FCSTD DOCUMENT  (FreeCAD 1.0R39109 (Git))
Label: Vista frontal
License: All rights reserved
LicenseURL: https://en.wikipedia.org/wiki/All_rights_reserved
objects: TechDraw::DrawSVGTemplate×1, TechDraw::DrawPage×1, Sketcher::SketchObject×1
note: 2 computed .brp shape members not serialized (recipe doc carries the construction recipe); baked Part::Feature solids carry a one-line shape summary decoded from their .brp

FEATURE [TechDraw::DrawSVGTemplate] Template  label="Plantilla"
  EditableTexts = approval_person=N/A; creator=Carlos E.; date_of_issue=11/3/25; document_status=In preparation; document_type=Assembly Drawing; drawing_number=DN; general_tolerances=ISO 2768-m; language_code=ES; part_material=Stainless steel Mat.No. 1.4301; responsible_department=RD; revision_index=AAA; sheet_number=1 / 1; sheet_scale=1 : 1; title=Interior de la cabina
  Height = 297
  Orientation = 1
  Template = C:/Program Files/FreeCAD 1.0/data/Mod/TechDraw/Templates/A3_Landscape_ISO5457_advanced.svg
  Width = 420
FEATURE [TechDraw::DrawPage] Page  label="Página"
  KeepUpdated = true
  NextBalloonIndex = 1
  ProjectionType = 0
  Template = -> Template
FEATURE [Sketcher::SketchObject] Sketch
  ArcFitTolerance = 1e-06
  FullyConstrained = false
  MakeInternals = false
  Placement = pos=(0,0,0) rot=(1,0,0;1.5708rad)
  sketch-geometry (86):
    g0: LineSegment StartX=0 StartY=0 StartZ=0 EndX=70.5 EndY=0 EndZ=0
    g1: LineSegment StartX=70.5 StartY=0 StartZ=0 EndX=70.5 EndY=14 EndZ=0
    g2: LineSegment StartX=70.5 StartY=14 StartZ=0 EndX=0 EndY=14 EndZ=0
    g3: LineSegment StartX=0 StartY=14 StartZ=0 EndX=0 EndY=0 EndZ=0
    g4: LineSegment [constr] StartX=70.5 StartY=0 StartZ=0 EndX=100 EndY=0 EndZ=0
    g5: LineSegment [constr] StartX=35.25 StartY=0 StartZ=0 EndX=35.25 EndY=105.536 EndZ=0
    g6: GeomPoint [constr] X=35.25 Y=14 Z=0
    g7: LineSegment StartX=35.25 StartY=14 StartZ=0 EndX=35.25 EndY=36.9 EndZ=0
    g8: LineSegment StartX=35.25 StartY=36.9 StartZ=0 EndX=-13.75 EndY=36.9 EndZ=0
    g9: LineSegment StartX=-13.75 StartY=36.9 StartZ=0 EndX=-13.75 EndY=14 EndZ=0
    g10: LineSegment StartX=-13.75 StartY=14 StartZ=0 EndX=35.25 EndY=14 EndZ=0
    g11: LineSegment StartX=35.25 StartY=14 StartZ=0 EndX=85.25 EndY=14 EndZ=0
    g12: LineSegment StartX=85.25 StartY=14 StartZ=0 EndX=85.25 EndY=36.9 EndZ=0
    g13: LineSegment StartX=85.25 StartY=36.9 StartZ=0 EndX=35.25 EndY=36.9 EndZ=0
    g14: LineSegment StartX=35.25 StartY=36.9 StartZ=0 EndX=35.25 EndY=14 EndZ=0
    g15: LineSegment [constr] StartX=85.25 StartY=36.47 StartZ=0 EndX=85.25 EndY=-0.43 EndZ=0
    g16: LineSegment StartX=85.25 StartY=2.9 StartZ=0 EndX=106.25 EndY=2.9 EndZ=0
    g17: LineSegment StartX=106.25 StartY=2.9 StartZ=0 EndX=106.25 EndY=36.9 EndZ=0
    g18: LineSegment StartX=106.25 StartY=36.9 StartZ=0 EndX=85.25 EndY=36.9 EndZ=0
    g19: LineSegment StartX=97.9545 StartY=26.7658 StartZ=0 EndX=105.58 EndY=26.7658 EndZ=0
    g20: LineSegment StartX=105.58 StartY=26.7658 StartZ=0 EndX=105.58 EndY=28.7188 EndZ=0
    g21: LineSegment StartX=105.58 StartY=28.7188 StartZ=0 EndX=97.9545 EndY=28.7188 EndZ=0
    g22: LineSegment StartX=97.9545 StartY=28.7188 StartZ=0 EndX=97.9545 EndY=26.7658 EndZ=0
    g23: LineSegment StartX=86.9421 StartY=33.4519 StartZ=0 EndX=93.2352 EndY=33.4519 EndZ=0
    g24: LineSegment StartX=93.2352 StartY=33.4519 StartZ=0 EndX=93.2352 EndY=35.4978 EndZ=0
    g25: LineSegment StartX=93.2352 StartY=35.4978 StartZ=0 EndX=86.9421 EndY=35.4978 EndZ=0
    g26: LineSegment StartX=86.9421 StartY=35.4978 StartZ=0 EndX=86.9421 EndY=33.4519 EndZ=0
    g27: LineSegment StartX=86.8307 StartY=26.9518 StartZ=0 EndX=96.1875 EndY=26.9518 EndZ=0
    g28: LineSegment StartX=96.1875 StartY=26.9518 StartZ=0 EndX=96.1875 EndY=28.6258 EndZ=0
    g29: LineSegment StartX=96.1875 StartY=28.6258 StartZ=0 EndX=86.8307 EndY=28.6258 EndZ=0
    g30: LineSegment StartX=86.8307 StartY=28.6258 StartZ=0 EndX=86.8307 EndY=26.9518 EndZ=0
    g31: Circle CenterX=96.5698 CenterY=34.2693 CenterZ=0 NormalX=0 NormalY=0 NormalZ=1 AngleXU=0 Radius=0.926737
    g32: Circle CenterX=103.395 CenterY=34.3247 CenterZ=0 NormalX=0 NormalY=0 NormalZ=1 AngleXU=0 Radius=1.37288
    g33: ArcOfCircle CenterX=98.9063 CenterY=31.1454 CenterZ=0 NormalX=0 NormalY=0 NormalZ=1 AngleXU=0 Radius=0.623395 StartAngle=1.5708 EndAngle=4.71239
    g34: ArcOfCircle CenterX=102.21 CenterY=31.1454 CenterZ=0 NormalX=0 NormalY=0 NormalZ=1 AngleXU=0 Radius=0.623395 StartAngle=4.71239 EndAngle=7.85398
    g35: LineSegment StartX=98.9063 StartY=31.7688 StartZ=0 EndX=102.21 EndY=31.7688 EndZ=0
    g36: LineSegment StartX=98.9063 StartY=30.522 StartZ=0 EndX=102.21 EndY=30.522 EndZ=0
    g37: LineSegment StartX=87.688 StartY=31.1722 StartZ=0 EndX=87.688 EndY=29.954 EndZ=0
    g38: LineSegment StartX=87.688 StartY=29.954 StartZ=0 EndX=89.2869 EndY=29.954 EndZ=0
    g39: LineSegment StartX=89.2869 StartY=29.954 StartZ=0 EndX=89.2869 EndY=31.1722 EndZ=0
    g40: LineSegment StartX=89.2869 StartY=31.1722 StartZ=0 EndX=87.688 EndY=31.1722 EndZ=0
    g41: LineSegment StartX=93.4747 StartY=31.4006 StartZ=0 EndX=91.3427 EndY=31.4006 EndZ=0
    g42: LineSegment StartX=91.3427 StartY=31.4006 StartZ=0 EndX=91.3427 EndY=30.0301 EndZ=0
    g43: LineSegment StartX=91.3427 StartY=30.0301 StartZ=0 EndX=93.4747 EndY=30.0301 EndZ=0
    g44: LineSegment StartX=93.4747 StartY=30.0301 StartZ=0 EndX=93.4747 EndY=31.4006 EndZ=0
    g45: LineSegment StartX=86.9179 StartY=23.4642 StartZ=0 EndX=86.9179 EndY=21.8832 EndZ=0
    g46: LineSegment StartX=86.9179 StartY=21.8832 StartZ=0 EndX=96.6828 EndY=21.8832 EndZ=0
    g47: LineSegment StartX=96.6828 StartY=21.8832 StartZ=0 EndX=96.6828 EndY=23.4642 EndZ=0
    g48: LineSegment StartX=96.6828 StartY=23.4642 StartZ=0 EndX=86.9179 EndY=23.4642 EndZ=0
    g49: LineSegment StartX=87.533 StartY=4.1575 StartZ=0 EndX=89.5902 EndY=4.1575 EndZ=0
    g50: LineSegment StartX=89.5902 StartY=4.1575 StartZ=0 EndX=89.5902 EndY=7.96019 EndZ=0
    g51: LineSegment StartX=89.5902 StartY=7.96019 StartZ=0 EndX=87.533 EndY=7.96019 EndZ=0
    g52: LineSegment StartX=87.533 StartY=7.96019 StartZ=0 EndX=87.533 EndY=4.1575 EndZ=0
    g53: LineSegment StartX=93.5175 StartY=6.46405 StartZ=0 EndX=93.5175 EndY=5.71598 EndZ=0
    g54: LineSegment StartX=93.5175 StartY=5.71598 StartZ=0 EndX=95.8864 EndY=5.71598 EndZ=0
    g55: LineSegment StartX=95.8864 StartY=5.71598 StartZ=0 EndX=95.8864 EndY=6.46405 EndZ=0
    g56: LineSegment StartX=95.8864 StartY=6.46405 StartZ=0 EndX=93.5175 EndY=6.46405 EndZ=0
    g57: LineSegment StartX=97.3202 StartY=6.65107 StartZ=0 EndX=97.3202 EndY=5.5913 EndZ=0
    g58: LineSegment StartX=97.3202 StartY=5.5913 StartZ=0 EndX=100.811 EndY=5.5913 EndZ=0
    g59: LineSegment StartX=100.811 StartY=5.5913 StartZ=0 EndX=100.811 EndY=6.65107 EndZ=0
    g60: LineSegment StartX=100.811 StartY=6.65107 StartZ=0 EndX=97.3202 EndY=6.65107 EndZ=0
    g61: Circle CenterX=103.766 CenterY=5.83681 CenterZ=0 NormalX=0 NormalY=0 NormalZ=1 AngleXU=0 Radius=1.37146
    g62: Circle CenterX=89.1538 CenterY=12.1369 CenterZ=0 NormalX=0 NormalY=0 NormalZ=1 AngleXU=0 Radius=1.87018
    g63: Circle CenterX=94.0162 CenterY=11.7005 CenterZ=0 NormalX=0 NormalY=0 NormalZ=1 AngleXU=0 Radius=0.872749
    g64: Circle CenterX=97.3826 CenterY=11.7629 CenterZ=0 NormalX=0 NormalY=0 NormalZ=1 AngleXU=0 Radius=0.758389
    g65: Circle CenterX=100.001 CenterY=11.8252 CenterZ=0 NormalX=0 NormalY=0 NormalZ=1 AngleXU=0 Radius=0.688557
    g66: Circle CenterX=102.37 CenterY=11.9499 CenterZ=0 NormalX=0 NormalY=0 NormalZ=1 AngleXU=0 Radius=0.819944
    g67: LineSegment StartX=99.1281 StartY=24.2307 StartZ=0 EndX=99.1281 EndY=21.1761 EndZ=0
    g68: LineSegment StartX=99.1281 StartY=21.1761 StartZ=0 EndX=100.998 EndY=21.1761 EndZ=0
    g69: LineSegment StartX=100.998 StartY=21.1761 StartZ=0 EndX=100.998 EndY=24.2307 EndZ=0
    g70: LineSegment StartX=100.998 StartY=24.2307 StartZ=0 EndX=99.1281 EndY=24.2307 EndZ=0
    g71: LineSegment StartX=103.18 StartY=24.4177 StartZ=0 EndX=103.18 EndY=20.615 EndZ=0
    g72: LineSegment StartX=103.18 StartY=20.615 StartZ=0 EndX=104.863 EndY=20.615 EndZ=0
    g73: LineSegment StartX=104.863 StartY=20.615 StartZ=0 EndX=104.863 EndY=24.4177 EndZ=0
    g74: LineSegment StartX=104.863 StartY=24.4177 StartZ=0 EndX=103.18 EndY=24.4177 EndZ=0
    g75: Circle CenterX=103.741 CenterY=16.376 CenterZ=0 NormalX=0 NormalY=0 NormalZ=1 AngleXU=0 Radius=1.45532
    g76: Circle CenterX=100.063 CenterY=16.5007 CenterZ=0 NormalX=0 NormalY=0 NormalZ=1 AngleXU=0 Radius=0.710776
    g77: LineSegment StartX=87.9693 StartY=19.3059 StartZ=0 EndX=87.9693 EndY=16.3136 EndZ=0
    g78: LineSegment StartX=87.9693 StartY=16.3136 StartZ=0 EndX=89.5278 EndY=16.3136 EndZ=0
    g79: LineSegment StartX=89.5278 StartY=16.3136 StartZ=0 EndX=89.5278 EndY=19.3059 EndZ=0
    g80: LineSegment StartX=89.5278 StartY=19.3059 StartZ=0 EndX=87.9693 EndY=19.3059 EndZ=0
    g81: LineSegment StartX=91.024 StartY=18.3085 StartZ=0 EndX=91.024 EndY=16.937 EndZ=0
    g82: LineSegment StartX=91.024 StartY=16.937 StartZ=0 EndX=97.3826 EndY=16.937 EndZ=0
    g83: LineSegment StartX=97.3826 StartY=16.937 StartZ=0 EndX=97.3826 EndY=18.3085 EndZ=0
    g84: LineSegment StartX=97.3826 StartY=18.3085 StartZ=0 EndX=91.024 EndY=18.3085 EndZ=0
    g85: LineSegment StartX=85.25 StartY=36.9 StartZ=0 EndX=85.25 EndY=2.9 EndZ=0
  constraints (159):
    c: Coincident(g0,g1)
    c: Coincident(g1,g2)
    c: Coincident(g2,g3)
    c: Coincident(g3,g0)
    c: Horizontal(g0)
    c: Horizontal(g2)
    c: Vertical(g1)
    c: Vertical(g3)
    c: Distance(g1,g3) = 70.5
    c: Distance(g0,g2) = 14
    c: Coincident(g0,g-1)
    c: Distance(g4) = 29.5
    c: Coincident(g4,g0)
    c: PointOnObject(g4,g-1)
    c: Symmetric(g0,g0,g5)
    c: Vertical(g5)
    c: Symmetric(g2,g2,g6)
    c: Coincident(g7,g8)
    c: Coincident(g8,g9)
    c: Coincident(g9,g10)
    c: Coincident(g10,g7)
    c: Vertical(g7)
    c: Vertical(g9)
    c: Horizontal(g8)
    c: Horizontal(g10)
    c: Distance(g7,g9) = 49
    c: Distance(g8,g10) = 22.9
    c: Coincident(g7,g6)
    c: Coincident(g11,g12)
    c: Coincident(g12,g13)
    c: Coincident(g13,g14)
    c: Coincident(g14,g11)
    c: Horizontal(g11)
    c: Horizontal(g13)
    c: Vertical(g12)
    c: Vertical(g14)
    c: Distance(g11,g13) = 22.9
    c: Coincident(g11,g6)
    c: Vertical(g15)
    c: Coincident(g16,g17)
    c: Coincident(g17,g18)
    c: Coincident(g18,g85)
    c: Coincident(g85,g16)
    c: Horizontal(g16)
    c: Horizontal(g18)
    c: Vertical(g17)
    c: Vertical(g85)
    c: Distance(g17,g85) = 21
    c: Distance(g16,g18) = 34
    c: Horizontal(g19)
    c: Coincident(g19,g20)
    c: Vertical(g20)
    c: Coincident(g20,g21)
    c: Horizontal(g21)
    c: Coincident(g21,g22)
    c: Coincident(g22,g19)
    c: Vertical(g22)
    c: Horizontal(g23)
    c: Coincident(g23,g24)
    c: Vertical(g24)
    c: Coincident(g24,g25)
    c: Horizontal(g25)
    c: Coincident(g25,g26)
    c: Coincident(g26,g23)
    c: Vertical(g26)
    c: Horizontal(g27)
    c: Coincident(g27,g28)
    c: Vertical(g28)
    c: Coincident(g28,g29)
    c: Horizontal(g29)
    c: Coincident(g29,g30)
    c: Coincident(g30,g27)
    c: Vertical(g30)
    c: Tangent(g33,g35) = 1.5708
    c: Tangent(g33,g36) = -1.5708
    c: Tangent(g34,g35) = 1.5708
    c: Tangent(g34,g36) = -1.5708
    c: Equal(g33,g34)
    c: Horizontal(g36)
    c: Coincident(g37,g38)
    c: Coincident(g38,g39)
    c: Coincident(g39,g40)
    c: Coincident(g40,g37)
    c: Vertical(g37)
    c: Vertical(g39)
    c: Horizontal(g38)
    c: Horizontal(g40)
    c: Coincident(g41,g42)
    c: Coincident(g42,g43)
    c: Coincident(g43,g44)
    c: Coincident(g44,g41)
    c: Horizontal(g41)
    c: Horizontal(g43)
    c: Vertical(g42)
    c: Vertical(g44)
    c: Coincident(g45,g46)
    c: Coincident(g46,g47)
    c: Coincident(g47,g48)
    c: Coincident(g48,g45)
    c: Vertical(g45)
    c: Vertical(g47)
    c: Horizontal(g46)
    c: Horizontal(g48)
    c: Coincident(g49,g50)
    c: Coincident(g50,g51)
    c: Coincident(g51,g52)
    c: Coincident(g52,g49)
    c: Horizontal(g49)
    c: Horizontal(g51)
    c: Vertical(g50)
    c: Vertical(g52)
    c: Coincident(g53,g54)
    c: Coincident(g54,g55)
    c: Coincident(g55,g56)
    c: Coincident(g56,g53)
    c: Vertical(g53)
    c: Vertical(g55)
    c: Horizontal(g54)
    c: Horizontal(g56)
    c: Coincident(g57,g58)
    c: Coincident(g58,g59)
    c: Coincident(g59,g60)
    c: Coincident(g60,g57)
    c: Vertical(g57)
    c: Vertical(g59)
    c: Horizontal(g58)
    c: Horizontal(g60)
    c: Coincident(g67,g68)
    c: Coincident(g68,g69)
    c: Coincident(g69,g70)
    c: Coincident(g70,g67)
    c: Vertical(g67)
    c: Vertical(g69)
    c: Horizontal(g68)
    c: Horizontal(g70)
    c: Coincident(g71,g72)
    c: Coincident(g72,g73)
    c: Coincident(g73,g74)
    c: Coincident(g74,g71)
    c: Vertical(g71)
    c: Vertical(g73)
    c: Horizontal(g72)
    c: Horizontal(g74)
    c: Coincident(g77,g78)
    c: Coincident(g78,g79)
    c: Coincident(g79,g80)
    c: Coincident(g80,g77)
    c: Vertical(g77)
    c: Vertical(g79)
    c: Horizontal(g78)
    c: Horizontal(g80)
    c: Coincident(g81,g82)
    c: Coincident(g82,g83)
    c: Coincident(g83,g84)
    c: Coincident(g84,g81)
    c: Vertical(g81)
    c: Vertical(g83)
    c: Horizontal(g82)
    c: Horizontal(g84)
